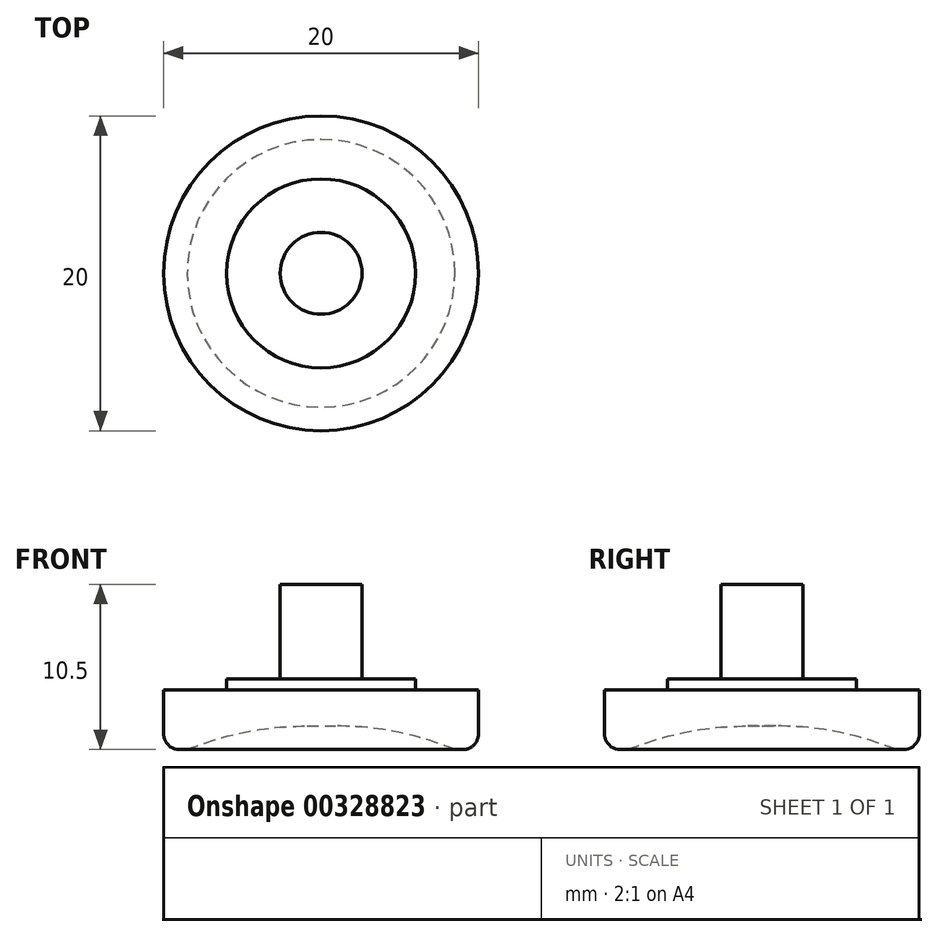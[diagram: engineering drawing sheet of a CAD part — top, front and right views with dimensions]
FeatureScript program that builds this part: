
annotation { "Feature Type Name" : "Feature", "Feature Type Description" : "" }
export const myFeature = defineFeature(function(context is Context, id is Id, definition is map)
    precondition{}
    {
        {
            var Q0;
            Q0=qCreatedBy(makeId("Top.planeOp"),FACE);
            var sketch = newSketch(context, id + "F0", { "sketchPlane" : qUnion([Q0])});
            skCircle(sketch, "E0", {"center": v(-11.32, 20.52) * mm, "radius": 10 * mm});
            skCircle(sketch, "E1", {"center": v(-11.32, 20.52) * mm, "radius": 2.6 * mm});
            skCircle(sketch, "E2", {"center": v(-11.32, 20.52) * mm, "radius": 6 * mm});
            skSolve(sketch);
        }
        {
            var Q0;
            Q0=makeQuery(id+"F0.imprint","IMPRINT",FACE,{"disambiguationData":[TD([[makeQuery(id+"F0.imprint","IMPRINT",EDGE,{"derivedFrom":sQuery(id+"F0.wireOp",EDGE,"E0")}),1.0]])]});
            extrude(context, id + "F1", {"entities" : qUnion([Q0]), "depth" : 4 * mm});
        }
        {
            var Q0;
            Q0=makeQuery(id+"F0.imprint","IMPRINT",FACE,{"disambiguationData":[TD([[makeQuery(id+"F0.imprint","IMPRINT",EDGE,{"derivedFrom":sQuery(id+"F0.wireOp",EDGE,"E1")}),-1.0]])]});
            extrude(context, id + "F2", {"entities" : qUnion([Q0]), "operationType" : NewBodyOperationType.ADD, "depth" : 4.5 * mm});
        }
        {
            var Q0;
            Q0=makeQuery(id+"F0.imprint","IMPRINT",FACE,{"disambiguationData":[TD([[makeQuery(id+"F0.imprint","IMPRINT",EDGE,{"derivedFrom":sQuery(id+"F0.wireOp",EDGE,"E1")}),1.0]])]});
            extrude(context, id + "F3", {"entities" : qUnion([Q0]), "operationType" : NewBodyOperationType.ADD, "depth" : 10.5 * mm});
        }
        {
            var Q0;
            {var subQ0=sQuery(id+"F0.wireOp",EDGE,"E1");var subQ1=sQuery(id+"F0.wireOp",EDGE,"E2");Q0=makeQuery(id+"F3.boolean.opBoolean","MERGE",FACE,{"derivedFrom":[makeQuery(id+"F2.boolean.opBoolean","MERGE",FACE,{"derivedFrom":[makeQuery(id+"F1.opExtrude","CAP_FACE",FACE,{"disambiguationData":[OSD([sQuery(id+"F0.wireOp",EDGE,"E0"),subQ1])],"isStart":true}),makeQuery(id+"F2.opExtrude","CAP_FACE",FACE,{"disambiguationData":[OSD([subQ0,subQ1])],"isStart":true})]}),makeQuery(id+"F3.opExtrude","CAP_FACE",FACE,{"disambiguationData":[OSD([subQ0])],"isStart":true})]});}
            var sketch = newSketch(context, id + "F4", { "sketchPlane" : qUnion([Q0])});
            skCircle(sketch, "E3", {"center": v(-11.32, -20.52) * mm, "radius": 8.5 * mm});
            skSolve(sketch);
        }
        {
            var Q0;
            Q0=makeQuery(id+"F4.imprint","IMPRINT",FACE,{"disambiguationData":[TD([[makeQuery(id+"F4.imprint","IMPRINT",EDGE,{"derivedFrom":sQuery(id+"F4.wireOp",EDGE,"E3")}),1.0]])]});
            extrude(context, id + "F5", {"entities" : qUnion([Q0]), "operationType" : NewBodyOperationType.REMOVE, "oppositeDirection" : true, "depth" : 1.5 * mm});
        }
        {
            var Q0;
            Q0=makeQuery(id+"F5.boolean.opBoolean","COPY",EDGE,{"derivedFrom":makeQuery(id+"F5.opExtrude","CAP_EDGE",EDGE,{"disambiguationData":[OSD([sQuery(id+"F4.wireOp",EDGE,"E3")])],"isStart":false})});
            fillet(context, id + "F6", {"entities" : qUnion([Q0]), "radius" : 20 * mm, "tangentPropagation" : true, "allowEdgeOverflow" : false});
        }
        {
            var Q0;
            Q0=makeQuery(id+"F1.opExtrude","CAP_EDGE",EDGE,{"disambiguationData":[OSD([sQuery(id+"F0.wireOp",EDGE,"E0")])],"isStart":true});
            fillet(context, id + "F7", {"entities" : qUnion([Q0]), "radius" : 1 * mm, "tangentPropagation" : true, "allowEdgeOverflow" : false});
        }
        {
            var Q0;
            Q0=makeQuery(id+"F1.opExtrude","CAP_FACE",FACE,{"disambiguationData":[OSD([sQuery(id+"F0.wireOp",EDGE,"E0"),sQuery(id+"F0.wireOp",EDGE,"E2")])],"isStart":false});
            extrude(context, id + "F8", {"entities" : qUnion([Q0]), "operationType" : NewBodyOperationType.REMOVE, "oppositeDirection" : true, "depth" : 0.2 * mm, "offsetDistance" : 25 * mm});
        }
    });
